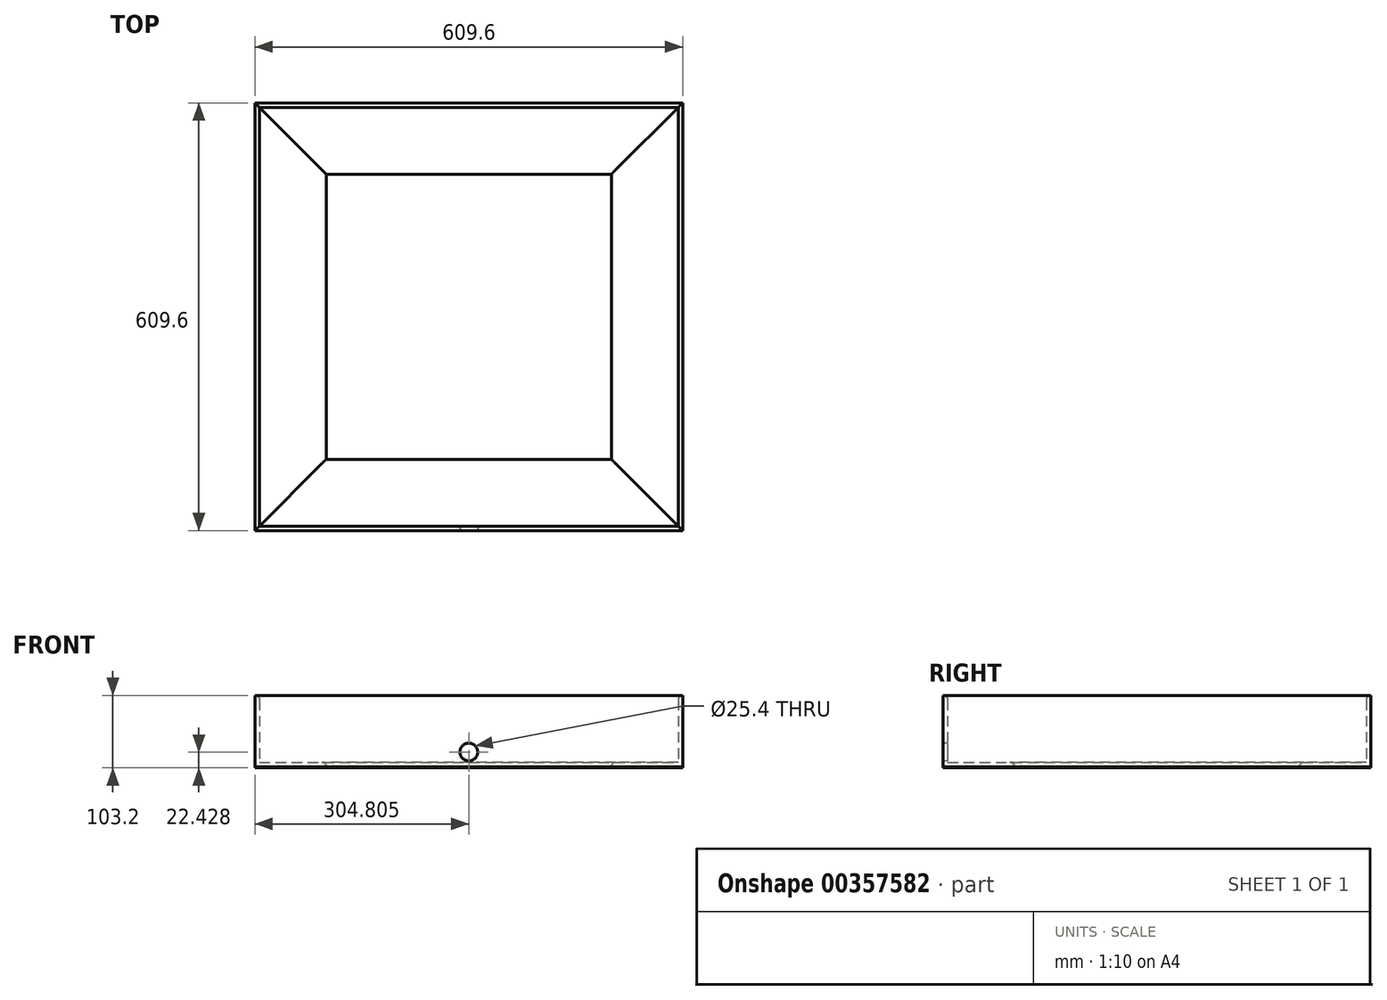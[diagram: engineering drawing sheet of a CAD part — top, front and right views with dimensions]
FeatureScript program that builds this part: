
annotation { "Feature Type Name" : "Feature", "Feature Type Description" : "" }
export const myFeature = defineFeature(function(context is Context, id is Id, definition is map)
    precondition{}
    {
        {
            var Q0;
            Q0=qCreatedBy(makeId("Top.planeOp"),FACE);
            var sketch = newSketch(context, id + "F0", { "sketchPlane" : qUnion([Q0])});
            skLineSegment(sketch, "E0.bottom", {"start": v(-84.57, 40.83) * mm, "end": v(321.83, 40.83) * mm});
            skLineSegment(sketch, "E0.top", {"start": v(-186.17, -60.77) * mm, "end": v(423.43, -60.77) * mm});
            skLineSegment(sketch, "E1", {"start": v(-186.17, -60.77) * mm, "end": v(-84.57, 40.83) * mm});
            skLineSegment(sketch, "E2", {"start": v(423.43, -60.77) * mm, "end": v(321.83, 40.83) * mm});
            skPoint(sketch, "E0.left.start.orphan", {"position": v(-186.17, 40.83) * mm});
            skSolve(sketch);
        }
        {
            var Q0;
            Q0 = qSketchRegion(id + "F0", true);
            extrude(context, id + "F1", {"entities" : qUnion([Q0]), "depth" : 6.35 * mm});
        }
        {
            var Q0;
            Q0=qCreatedBy(makeId("Top.planeOp"),FACE);
            var sketch = newSketch(context, id + "F2", { "sketchPlane" : qUnion([Q0])});
            skLineSegment(sketch, "E3.0", {"start": v(-186.17, -60.77) * mm, "end": v(423.43, -60.77) * mm});
            skLineSegment(sketch, "E4.0", {"start": v(-186.17, -60.77) * mm, "end": v(-179.82, -54.42) * mm});
            skLineSegment(sketch, "E5.0", {"start": v(423.43, -60.77) * mm, "end": v(417.08, -54.42) * mm});
            skLineSegment(sketch, "E6", {"start": v(-179.82, -54.42) * mm, "end": v(417.08, -54.42) * mm});
            skPoint(sketch, "E7.orphan", {"position": v(-84.57, 40.83) * mm});
            skPoint(sketch, "E8.orphan", {"position": v(321.83, 40.83) * mm});
            skSolve(sketch);
        }
        {
            var Q0;
            Q0 = qSketchRegion(id + "F2", true);
            extrude(context, id + "F3", {"entities" : qUnion([Q0]), "operationType" : NewBodyOperationType.ADD, "depth" : 101.6 * mm});
        }
        {
            var Q0;
            Q0=makeQuery(id+"F1.opExtrude","CAP_EDGE",EDGE,{"disambiguationData":[OSD([sQuery(id+"F0.wireOp",EDGE,"E0.bottom")])],"isStart":false});
            var Q1;
            Q1=makeQuery(id+"F3.opExtrude","CAP_EDGE",EDGE,{"disambiguationData":[OSD([sQuery(id+"F2.wireOp",EDGE,"E6")])],"isStart":false});
            fillet(context, id + "F4", {"entities" : qUnion([Q0, Q1]), "radius" : 6.1 * mm, "tangentPropagation" : true, "allowEdgeOverflow" : false});
        }
        {
            var Q0;
            Q0=qCreatedBy(makeId("Top.planeOp"),FACE);
            var sketch = newSketch(context, id + "F5", { "sketchPlane" : qUnion([Q0])});
            skLineSegment(sketch, "E9.0", {"start": v(-179.82, -54.42) * mm, "end": v(118.63, 244.03) * mm, "construction": true});
            skLineSegment(sketch, "E10.0", {"start": v(417.08, -54.42) * mm, "end": v(118.63, 244.03) * mm, "construction": true});
            skPoint(sketch, "E11.orphan", {"position": v(-84.57, 40.83) * mm});
            skPoint(sketch, "E12.orphan", {"position": v(321.83, 40.83) * mm});
            skSolve(sketch);
        }
        {
            var Q0;
            Q0=qCreatedBy(makeId("Right.planeOp"),FACE);
            var Q1;
            Q1=sQuery(id+"F5.wireOp",VERTEX,"E10.0.end");
            cPlane(context, id + "F6", {"entities" : qUnion([Q0, Q1]), "cplaneType" : CPlaneType.PLANE_POINT, "offset" : 25.4 * mm, "width" : 152.4 * mm, "height" : 152.4 * mm});
        }
        {
            var Q0;
            Q0=qCreatedBy(id+"F6.planeOp",FACE);
            var sketch = newSketch(context, id + "F7", { "sketchPlane" : qUnion([Q0])});
            skPoint(sketch, "E13.0", {"position": v(244.03, 0) * mm});
            skLineSegment(sketch, "E14", {"start": v(244.03, 0) * mm, "end": v(244.03, 95.26) * mm, "construction": true});
            skSolve(sketch);
        }
        {
            var Q0;
            Q0=makeQuery(id+"F1.opExtrude","SWEPT_BODY",BODY,{"disambiguationData":[OSD([sQuery(id+"F0.wireOp",EDGE,"E0.bottom"),sQuery(id+"F0.wireOp",EDGE,"E0.top"),sQuery(id+"F0.wireOp",EDGE,"E1"),sQuery(id+"F0.wireOp",EDGE,"E2")])]});
            var Q1;
            Q1=sQuery(id+"F7.wireOp",EDGE,"E14");
            circularPattern(context, id + "F8", {"entities" : qUnion([Q0]), "axis" : qUnion([Q1]), "angle" : 360 * degree, "instanceCount" : 4, "equalSpace" : true});
        }
        {
            var Q0;
            Q0=qCreatedBy(makeId("Top.planeOp"),FACE);
            var sketch = newSketch(context, id + "F9", { "sketchPlane" : qUnion([Q0])});
            skPoint(sketch, "E15.0", {"position": v(118.63, 244.03) * mm});
            skLineSegment(sketch, "E16.bottom", {"start": v(-186.17, 548.83) * mm, "end": v(423.43, 548.83) * mm});
            skLineSegment(sketch, "E16.top", {"start": v(-186.17, -60.77) * mm, "end": v(423.43, -60.77) * mm});
            skLineSegment(sketch, "E16.left", {"start": v(-186.17, 548.83) * mm, "end": v(-186.17, -60.77) * mm});
            skLineSegment(sketch, "E16.right", {"start": v(423.43, 548.83) * mm, "end": v(423.43, -60.77) * mm});
            skSolve(sketch);
        }
        {
            var Q0;
            Q0 = qSketchRegion(id + "F9", true);
            extrude(context, id + "F10", {"entities" : qUnion([Q0]), "oppositeDirection" : true, "depth" : 1.6 * mm});
        }
        {
            var Q0;
            Q0=makeQuery(id+"F3.boolean.opBoolean","MERGE",FACE,{"derivedFrom":[makeQuery(id+"F1.opExtrude","SWEPT_FACE",FACE,{"disambiguationData":[OSD([sQuery(id+"F0.wireOp",EDGE,"E0.top")])]}),makeQuery(id+"F3.opExtrude","SWEPT_FACE",FACE,{"disambiguationData":[OSD([sQuery(id+"F2.wireOp",EDGE,"E3.0")])]})]});
            var sketch = newSketch(context, id + "F11", { "sketchPlane" : qUnion([Q0])});
            skLineSegment(sketch, "E17.0.0", {"start": v(-186.17, 0) * mm, "end": v(423.43, 0) * mm});
            skLineSegment(sketch, "E17.0.1", {"start": v(423.43, 0) * mm, "end": v(423.43, 101.6) * mm});
            skLineSegment(sketch, "E17.0.2", {"start": v(423.43, 101.6) * mm, "end": v(-186.17, 101.6) * mm});
            skLineSegment(sketch, "E17.0.3", {"start": v(-186.17, 101.6) * mm, "end": v(-186.17, 0) * mm});
            skPoint(sketch, "E18.0", {"position": v(118.63, 0) * mm});
            skLineSegment(sketch, "E19", {"start": v(118.63, 0) * mm, "end": v(118.63, 101.6) * mm, "construction": true});
            skPoint(sketch, "E19.endSnap0", {"position": v(118.63, 101.6) * mm});
            skPoint(sketch, "E20.orphan", {"position": v(118.63, 114.3) * mm});
            skLineSegment(sketch, "E21.0", {"start": v(417.08, 6.35) * mm, "end": v(-179.82, 6.35) * mm, "construction": true});
            skPoint(sketch, "E22", {"position": v(118.63, 20.83) * mm});
            skCircle(sketch, "E23", {"center": v(118.63, 20.83) * mm, "radius": 13.97 * mm});
            skSolve(sketch);
        }
        {
            var Q0;
            Q0=sQuery(id+"F11.wireOp",VERTEX,"E22");
            var Q1;
            Q1=makeQuery(id+"F1.opExtrude","SWEPT_BODY",BODY,{"disambiguationData":[OSD([sQuery(id+"F0.wireOp",EDGE,"E0.bottom"),sQuery(id+"F0.wireOp",EDGE,"E0.top"),sQuery(id+"F0.wireOp",EDGE,"E1"),sQuery(id+"F0.wireOp",EDGE,"E2")])]});
            hole(context, id + "F12", {"style" : HoleStyle.SIMPLE, "endStyle" : HoleEndStyle.THROUGH, "holeDiameter" : 25.4 * mm, "isTappedThrough" : true, "tappedDepth" : 12.7 * mm, "tapClearance" : 3, "locations" : qUnion([Q0]), "scope" : qUnion([Q1])});
        }
    });
